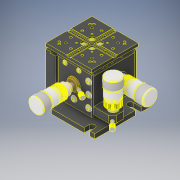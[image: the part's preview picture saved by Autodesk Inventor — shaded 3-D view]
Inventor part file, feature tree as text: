
AUTODESK INVENTOR PART (.ipt)
format: ipt  version: 2019 (Build 230136000, 136)  size: 4,489,728 bytes
history: native  units: in
note: dims shown in document units (in); Inventor stores cm internally (conversion verified against a paired STEP export)
features: other x3, plane x1
ambient origin geometry x8: Origin, YZ Plane, XZ Plane, XY Plane, X Axis, Y Axis, Z Axis, Center Point
bodies: Solid1 (feature_tree)
feature tree (4):
  plane  "Work Plane1"
  parser-record x1  (decoder bookkeeping rows leaked as tree rows — omitted from the tree; the rows remain in map.json)
  other  "Composite1"
  other  "Srf1"
